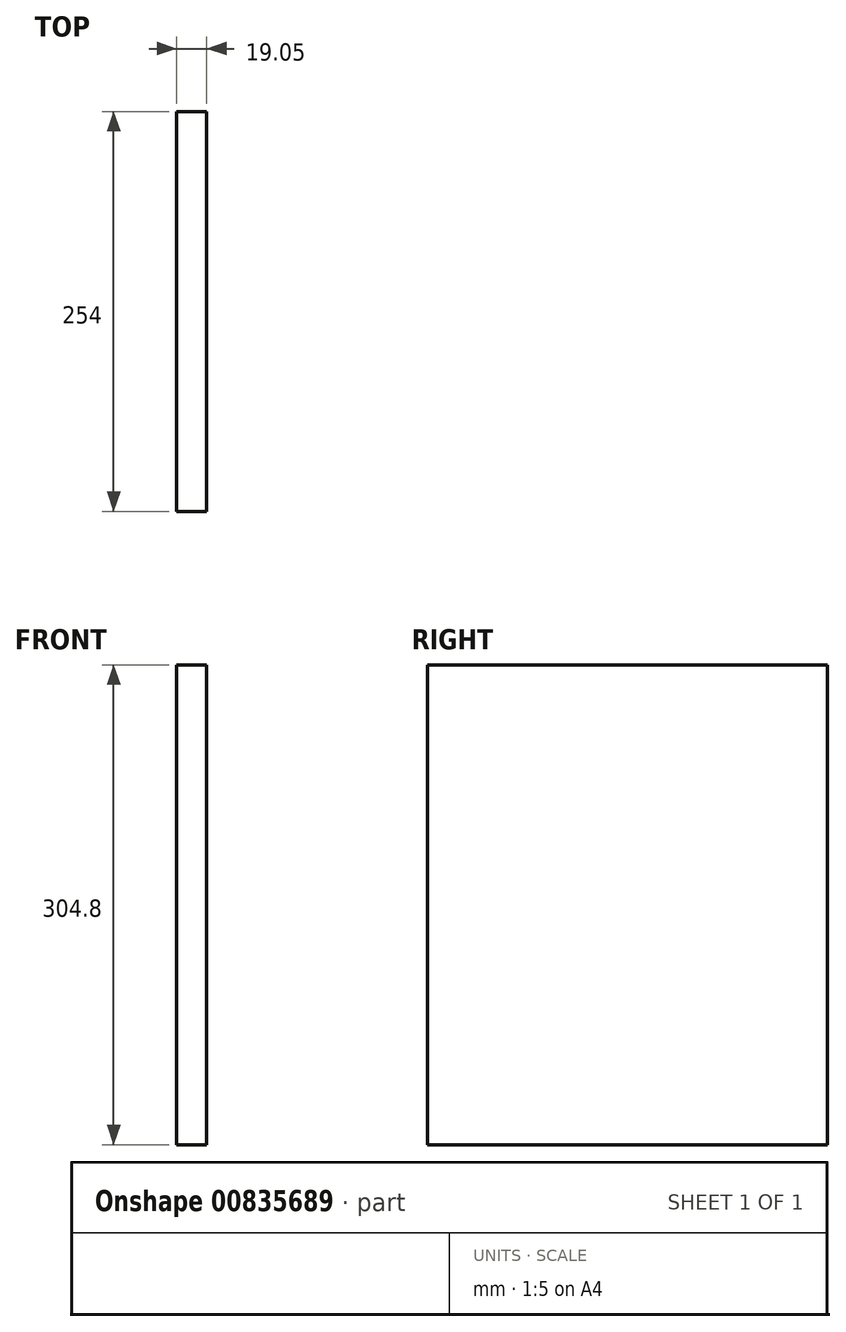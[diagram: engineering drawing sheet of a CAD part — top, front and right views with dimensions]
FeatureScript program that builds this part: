
annotation { "Feature Type Name" : "Feature", "Feature Type Description" : "" }
export const myFeature = defineFeature(function(context is Context, id is Id, definition is map)
    precondition{}
    {
        {
            var Q0;
            Q0=qCreatedBy(makeId("Right.planeOp"),FACE);
            var sketch = newSketch(context, id + "F0", { "sketchPlane" : qUnion([Q0])});
            skLineSegment(sketch, "E0.bottom", {"start": v(0, 0) * mm, "end": v(254, 0) * mm});
            skLineSegment(sketch, "E0.top", {"start": v(0, 304.8) * mm, "end": v(254, 304.8) * mm});
            skLineSegment(sketch, "E0.left", {"start": v(0, 0) * mm, "end": v(0, 304.8) * mm});
            skLineSegment(sketch, "E0.right", {"start": v(254, 0) * mm, "end": v(254, 304.8) * mm});
            skSolve(sketch);
        }
        {
            var Q0;
            Q0=qSketchRegion(id+"F0",true);
            extrude(context, id + "F1", {"entities" : qUnion([Q0]), "depth" : 19.05 * mm, "offsetDistance" : 25.4 * mm});
        }
    });
